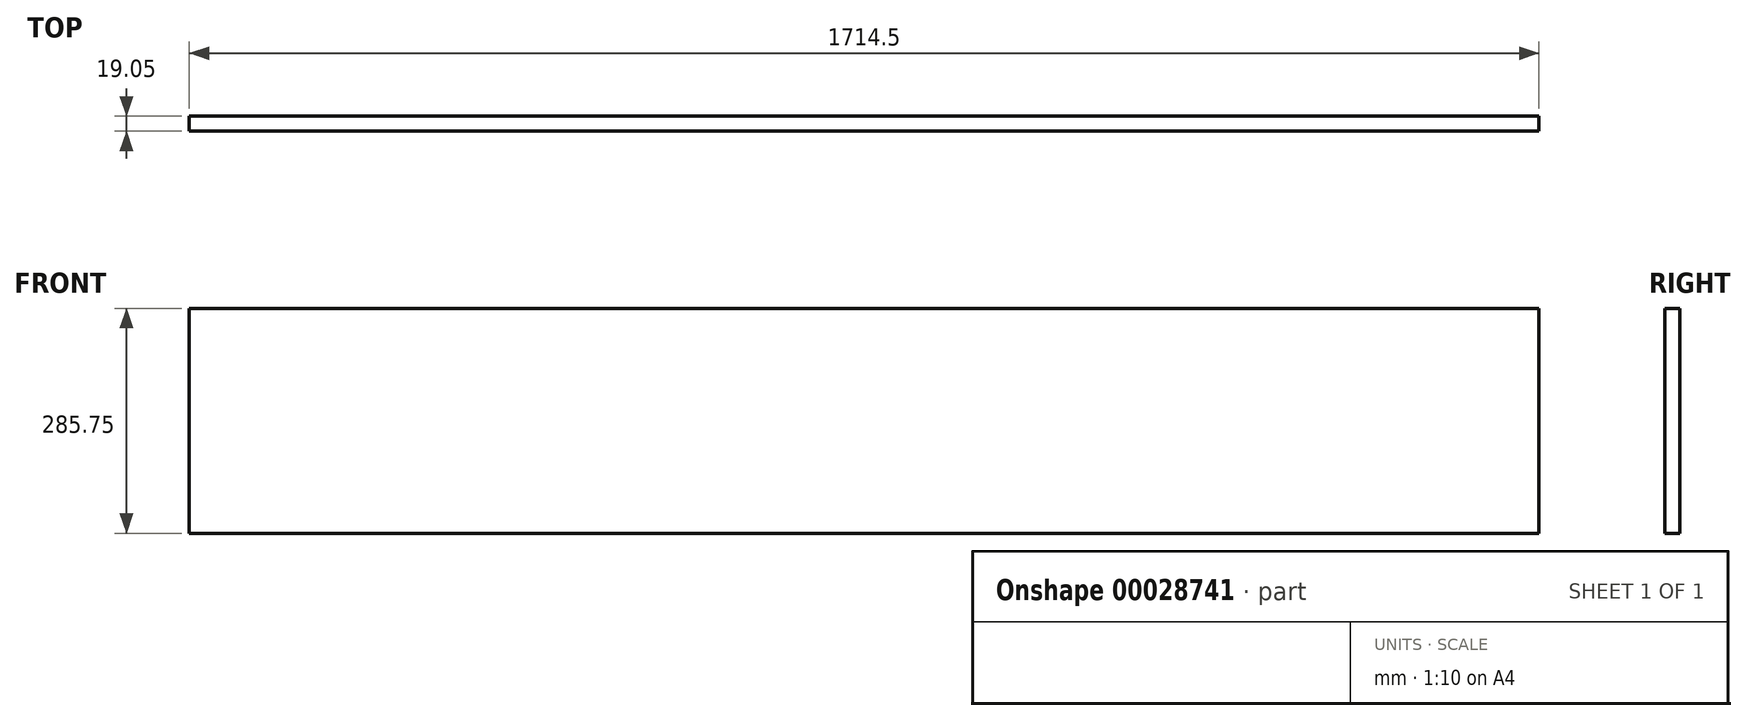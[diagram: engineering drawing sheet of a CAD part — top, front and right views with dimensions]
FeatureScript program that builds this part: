
annotation { "Feature Type Name" : "Feature", "Feature Type Description" : "" }
export const myFeature = defineFeature(function(context is Context, id is Id, definition is map)
    precondition{}
    {
        {
            var Q0;
            Q0=qCreatedBy(makeId("Front.planeOp"),FACE);
            var sketch = newSketch(context, id + "F0", { "sketchPlane" : qUnion([Q0])});
            skLineSegment(sketch, "E0.bottom", {"start": v(-861.42, 135.86) * mm, "end": v(853.08, 135.86) * mm});
            skLineSegment(sketch, "E0.top", {"start": v(-861.42, -149.89) * mm, "end": v(853.08, -149.89) * mm});
            skLineSegment(sketch, "E0.left", {"start": v(-861.42, 135.86) * mm, "end": v(-861.42, -149.89) * mm});
            skLineSegment(sketch, "E0.right", {"start": v(853.08, 135.86) * mm, "end": v(853.08, -149.89) * mm});
            skSolve(sketch);
        }
        {
            var Q0;
            Q0 = qSketchRegion(id + "F0", true);
            extrude(context, id + "F1", {"entities" : qUnion([Q0]), "depth" : 19.05 * mm});
        }
    });
